# Revit family: FAMILLE_COMPOSABLE_MOSAIC_FR
name_source: partatom
category: Equipement électrique
revit_build: Autodesk Revit 2017 (Build: 20190508_0315(x64)
units: mm (PartAtom-declared; Revit-internal decimal feet)

## family parameters
Basée sur le plan de construction = Non
Configuration du panneau = Deux colonnes, circuits au sein
Cote de connecteur circulaire = Utiliser le diamètre
Couper avec des vides une fois chargée = Non
Partagée = Oui
Point de calcul de pièce = Non
Toujours verticalement = Oui
Type d'élément = Tableau de raccordement

## types (20) — shared parameters
FONCTION MODULE 1 = CACHE_FR : CACHE
FONCTION RANG 2 MODULE 11 = VIDE_FR

## per-type parameters (varying)
- Type 1 _ 1 Module: DECALAGE X=22.5 mm  [stored 0.0738189 ft]; FONCTION MODULE 10=VIDE_FR; FONCTION MODULE 11=VIDE_FR; FONCTION MODULE 2=VIDE_FR; FONCTION MODULE 3=VIDE_FR; FONCTION MODULE 4=VIDE_FR; FONCTION MODULE 5=VIDE_FR; FONCTION MODULE 6=VIDE_FR; FONCTION MODULE 7=VIDE_FR; FONCTION MODULE 8=VIDE_FR; FONCTION MODULE 9=VIDE_FR; FONCTION RANG 2 MODULE 1=VIDE_FR; FONCTION RANG 2 MODULE 10=VIDE_FR; FONCTION RANG 2 MODULE 2=VIDE_FR; FONCTION RANG 2 MODULE 3=VIDE_FR; FONCTION RANG 2 MODULE 4=VIDE_FR; FONCTION RANG 2 MODULE 5=VIDE_FR; FONCTION RANG 2 MODULE 6=VIDE_FR; FONCTION RANG 2 MODULE 7=VIDE_FR; FONCTION RANG 2 MODULE 8=VIDE_FR; FONCTION RANG 2 MODULE 9=VIDE_FR; FONCTION RANG 3 MODULE 1=VIDE_FR; FONCTION RANG 3 MODULE 2=VIDE_FR; PLAQUE=PLAQUES_MOSAIC_FR : LEGRAND_MOSAIC_PLAQUE_1_MOD_BLANC_078801L.rfa; SUPPORT=SUPPORTS_UNIVERSELS_FR : LEGRAND_BATIBOX_SUPPORT_1_MOD_080250.rfa
- Type 2 _ 2 Modules: DECALAGE X=45 mm  [stored 0.147638 ft]; FONCTION MODULE 10=VIDE_FR; FONCTION MODULE 11=VIDE_FR; FONCTION MODULE 2=CACHE_FR : CACHE; FONCTION MODULE 3=VIDE_FR; FONCTION MODULE 4=VIDE_FR; FONCTION MODULE 5=VIDE_FR; FONCTION MODULE 6=VIDE_FR; FONCTION MODULE 7=VIDE_FR; FONCTION MODULE 8=VIDE_FR; FONCTION MODULE 9=VIDE_FR; FONCTION RANG 2 MODULE 1=VIDE_FR; FONCTION RANG 2 MODULE 10=VIDE_FR; FONCTION RANG 2 MODULE 2=VIDE_FR; FONCTION RANG 2 MODULE 3=VIDE_FR; FONCTION RANG 2 MODULE 4=VIDE_FR; FONCTION RANG 2 MODULE 5=VIDE_FR; FONCTION RANG 2 MODULE 6=VIDE_FR; FONCTION RANG 2 MODULE 7=VIDE_FR; FONCTION RANG 2 MODULE 8=VIDE_FR; FONCTION RANG 2 MODULE 9=VIDE_FR; FONCTION RANG 3 MODULE 1=VIDE_FR; FONCTION RANG 3 MODULE 2=VIDE_FR; PLAQUE=PLAQUES_MOSAIC_FR : LEGRAND_MOSAIC_PLAQUE_2_MOD_BLANC_078802L.rfa; SUPPORT=SUPPORTS_UNIVERSELS_FR : LEGRAND_BATIBOX_SUPPORT_1_POSTE_2_MOD_080251.rfa H
- Type 3 _ 3 Modules: DECALAGE X=67.5 mm  [stored 0.221457 ft]; FONCTION MODULE 10=VIDE_FR; FONCTION MODULE 11=VIDE_FR; FONCTION MODULE 2=CACHE_FR : CACHE; FONCTION MODULE 3=CACHE_FR : CACHE; FONCTION MODULE 4=VIDE_FR; FONCTION MODULE 5=VIDE_FR; FONCTION MODULE 6=VIDE_FR; FONCTION MODULE 7=VIDE_FR; FONCTION MODULE 8=VIDE_FR; FONCTION MODULE 9=VIDE_FR; FONCTION RANG 2 MODULE 1=VIDE_FR; FONCTION RANG 2 MODULE 10=VIDE_FR; FONCTION RANG 2 MODULE 2=VIDE_FR; FONCTION RANG 2 MODULE 3=VIDE_FR; FONCTION RANG 2 MODULE 4=VIDE_FR; FONCTION RANG 2 MODULE 5=VIDE_FR; FONCTION RANG 2 MODULE 6=VIDE_FR; FONCTION RANG 2 MODULE 7=VIDE_FR; FONCTION RANG 2 MODULE 8=VIDE_FR; FONCTION RANG 2 MODULE 9=VIDE_FR; FONCTION RANG 3 MODULE 1=VIDE_FR; FONCTION RANG 3 MODULE 2=VIDE_FR; PLAQUE=PLAQUES_MOSAIC_FR : LEGRAND_MOSAIC_PLAQUE_3_MOD_BLANC_078803L.rfa; SUPPORT=SUPPORTS_UNIVERSELS_FR : LEGRAND_BATIBOX_SUPPORT_3_MOD_080259.rfa H
- Type 4  _ 4 Modules: DECALAGE X=101.255 mm  [stored 0.332201 ft]; FONCTION MODULE 10=VIDE_FR; FONCTION MODULE 11=VIDE_FR; FONCTION MODULE 2=CACHE_FR : CACHE; FONCTION MODULE 3=CACHE_FR : CACHE; FONCTION MODULE 4=CACHE_FR : CACHE; FONCTION MODULE 5=VIDE_FR; FONCTION MODULE 6=VIDE_FR; FONCTION MODULE 7=VIDE_FR; FONCTION MODULE 8=VIDE_FR; FONCTION MODULE 9=VIDE_FR; FONCTION RANG 2 MODULE 1=VIDE_FR; FONCTION RANG 2 MODULE 10=VIDE_FR; FONCTION RANG 2 MODULE 2=VIDE_FR; FONCTION RANG 2 MODULE 3=VIDE_FR; FONCTION RANG 2 MODULE 4=VIDE_FR; FONCTION RANG 2 MODULE 5=VIDE_FR; FONCTION RANG 2 MODULE 6=VIDE_FR; FONCTION RANG 2 MODULE 7=VIDE_FR; FONCTION RANG 2 MODULE 8=VIDE_FR; FONCTION RANG 2 MODULE 9=VIDE_FR; FONCTION RANG 3 MODULE 1=VIDE_FR; FONCTION RANG 3 MODULE 2=VIDE_FR; PLAQUE=PLAQUES_MOSAIC_FR : LEGRAND_MOSAIC_PLAQUE_4_MOD_BLANC_078814L.rfa; SUPPORT=SUPPORTS_UNIVERSELS_FR : LEGRAND_BATIBOX_SUPPORT_2_POSTES_4_5_MOD_080252.rfa H
- Type 5  _ 5 Modules: DECALAGE X=112.5 mm  [stored 0.369094 ft]; FONCTION MODULE 10=VIDE_FR; FONCTION MODULE 11=VIDE_FR; FONCTION MODULE 2=CACHE_FR : CACHE; FONCTION MODULE 3=CACHE_FR : CACHE; FONCTION MODULE 4=CACHE_FR : CACHE; FONCTION MODULE 5=CACHE_FR : CACHE; FONCTION MODULE 6=VIDE_FR; FONCTION MODULE 7=VIDE_FR; FONCTION MODULE 8=VIDE_FR; FONCTION MODULE 9=VIDE_FR; FONCTION RANG 2 MODULE 1=VIDE_FR; FONCTION RANG 2 MODULE 10=VIDE_FR; FONCTION RANG 2 MODULE 2=VIDE_FR; FONCTION RANG 2 MODULE 3=VIDE_FR; FONCTION RANG 2 MODULE 4=VIDE_FR; FONCTION RANG 2 MODULE 5=VIDE_FR; FONCTION RANG 2 MODULE 6=VIDE_FR; FONCTION RANG 2 MODULE 7=VIDE_FR; FONCTION RANG 2 MODULE 8=VIDE_FR; FONCTION RANG 2 MODULE 9=VIDE_FR; FONCTION RANG 3 MODULE 1=VIDE_FR; FONCTION RANG 3 MODULE 2=VIDE_FR; PLAQUE=PLAQUES_MOSAIC_FR : LEGRAND_MOSAIC_PLAQUE_5_MOD_BLANC_078815L.rfa; SUPPORT=SUPPORTS_UNIVERSELS_FR : LEGRAND_BATIBOX_SUPPORT_2_POSTES_4_5_MOD_080252.rfa H
- Type 6 _ 2x2 Modules: DECALAGE X=112.5 mm  [stored 0.369094 ft]; FONCTION MODULE 10=VIDE_FR; FONCTION MODULE 11=VIDE_FR; FONCTION MODULE 2=CACHE_FR : CACHE; FONCTION MODULE 3=VIDE_FR; FONCTION MODULE 4=CACHE_FR : CACHE; FONCTION MODULE 5=CACHE_FR : CACHE; FONCTION MODULE 6=VIDE_FR; FONCTION MODULE 7=VIDE_FR; FONCTION MODULE 8=VIDE_FR; FONCTION MODULE 9=VIDE_FR; FONCTION RANG 2 MODULE 1=VIDE_FR; FONCTION RANG 2 MODULE 10=VIDE_FR; FONCTION RANG 2 MODULE 2=VIDE_FR; FONCTION RANG 2 MODULE 3=VIDE_FR; FONCTION RANG 2 MODULE 4=VIDE_FR; FONCTION RANG 2 MODULE 5=VIDE_FR; FONCTION RANG 2 MODULE 6=VIDE_FR; FONCTION RANG 2 MODULE 7=VIDE_FR; FONCTION RANG 2 MODULE 8=VIDE_FR; FONCTION RANG 2 MODULE 9=VIDE_FR; FONCTION RANG 3 MODULE 1=VIDE_FR; FONCTION RANG 3 MODULE 2=VIDE_FR; PLAQUE=PLAQUES_MOSAIC_FR : LEGRAND_MOSAIC_PLAQUE_2X2_MOD_BLANC_078804L.rfa; SUPPORT=SUPPORTS_UNIVERSELS_FR : LEGRAND_BATIBOX_SUPPORT_2_POSTES_4_5_MOD_080252.rfa H
- Type 9 _ 6 Modules: DECALAGE X=157.5 mm  [stored 0.516732 ft]; FONCTION MODULE 10=VIDE_FR; FONCTION MODULE 11=VIDE_FR; FONCTION MODULE 2=CACHE_FR : CACHE; FONCTION MODULE 3=CACHE_FR : CACHE; FONCTION MODULE 4=CACHE_FR : CACHE; FONCTION MODULE 5=CACHE_FR : CACHE; FONCTION MODULE 6=CACHE_FR : CACHE; FONCTION MODULE 7=VIDE_FR; FONCTION MODULE 8=VIDE_FR; FONCTION MODULE 9=VIDE_FR; FONCTION RANG 2 MODULE 1=VIDE_FR; FONCTION RANG 2 MODULE 10=VIDE_FR; FONCTION RANG 2 MODULE 2=VIDE_FR; FONCTION RANG 2 MODULE 3=VIDE_FR; FONCTION RANG 2 MODULE 4=VIDE_FR; FONCTION RANG 2 MODULE 5=VIDE_FR; FONCTION RANG 2 MODULE 6=VIDE_FR; FONCTION RANG 2 MODULE 7=VIDE_FR; FONCTION RANG 2 MODULE 8=VIDE_FR; FONCTION RANG 2 MODULE 9=VIDE_FR; FONCTION RANG 3 MODULE 1=VIDE_FR; FONCTION RANG 3 MODULE 2=VIDE_FR; PLAQUE=PLAQUES_MOSAIC_FR : LEGRAND_MOSAIC_PLAQUE_6_MOD_BLANC_078816L.rfa; SUPPORT=SUPPORTS_UNIVERSELS_FR : LEGRAND_BATIBOX_SUPPORT_3_POSTES_6_8_MOD_080253.rfa H
- Type. 10 _ 8 Modules: DECALAGE X=180 mm  [stored 0.590551 ft]; FONCTION MODULE 10=VIDE_FR; FONCTION MODULE 11=VIDE_FR; FONCTION MODULE 2=CACHE_FR : CACHE; FONCTION MODULE 3=CACHE_FR : CACHE; FONCTION MODULE 4=CACHE_FR : CACHE; FONCTION MODULE 5=CACHE_FR : CACHE; FONCTION MODULE 6=CACHE_FR : CACHE; FONCTION MODULE 7=CACHE_FR : CACHE; FONCTION MODULE 8=CACHE_FR : CACHE; FONCTION MODULE 9=VIDE_FR; FONCTION RANG 2 MODULE 1=VIDE_FR; FONCTION RANG 2 MODULE 10=VIDE_FR; FONCTION RANG 2 MODULE 2=VIDE_FR; FONCTION RANG 2 MODULE 3=VIDE_FR; FONCTION RANG 2 MODULE 4=VIDE_FR; FONCTION RANG 2 MODULE 5=VIDE_FR; FONCTION RANG 2 MODULE 6=VIDE_FR; FONCTION RANG 2 MODULE 7=VIDE_FR; FONCTION RANG 2 MODULE 8=VIDE_FR; FONCTION RANG 2 MODULE 9=VIDE_FR; FONCTION RANG 3 MODULE 1=VIDE_FR; FONCTION RANG 3 MODULE 2=VIDE_FR; PLAQUE=PLAQUES_MOSAIC_FR : LEGRAND_MOSAIC_PLAQUE_8_MOD_BLANC_078818L.rfa; SUPPORT=SUPPORTS_UNIVERSELS_FR : LEGRAND_BATIBOX_SUPPORT_3_POSTES_6_8_MOD_080253.rfa H
- Type. 11 _ 3x2 Modules: DECALAGE X=180 mm  [stored 0.590551 ft]; FONCTION MODULE 10=VIDE_FR; FONCTION MODULE 11=VIDE_FR; FONCTION MODULE 2=CACHE_FR : CACHE; FONCTION MODULE 3=VIDE_FR; FONCTION MODULE 4=CACHE_FR : CACHE; FONCTION MODULE 5=CACHE_FR : CACHE; FONCTION MODULE 6=VIDE_FR; FONCTION MODULE 7=CACHE_FR : CACHE; FONCTION MODULE 8=CACHE_FR : CACHE; FONCTION MODULE 9=VIDE_FR; FONCTION RANG 2 MODULE 1=VIDE_FR; FONCTION RANG 2 MODULE 10=VIDE_FR; FONCTION RANG 2 MODULE 2=VIDE_FR; FONCTION RANG 2 MODULE 3=VIDE_FR; FONCTION RANG 2 MODULE 4=VIDE_FR; FONCTION RANG 2 MODULE 5=VIDE_FR; FONCTION RANG 2 MODULE 6=VIDE_FR; FONCTION RANG 2 MODULE 7=VIDE_FR; FONCTION RANG 2 MODULE 8=VIDE_FR; FONCTION RANG 2 MODULE 9=VIDE_FR; FONCTION RANG 3 MODULE 1=VIDE_FR; FONCTION RANG 3 MODULE 2=VIDE_FR; PLAQUE=PLAQUES_MOSAIC_FR : LEGRAND_MOSAIC_PLAQUE_3X2_MOD_BLANC_078806L.rfa; SUPPORT=SUPPORTS_UNIVERSELS_FR : LEGRAND_BATIBOX_SUPPORT_3_POSTES_6_8_MOD_080253.rfa H
- Type. 13 _ 10 Modules: DECALAGE X=237.25 mm  [stored 0.778379 ft]; FONCTION MODULE 10=CACHE_FR : CACHE; FONCTION MODULE 11=VIDE_FR; FONCTION MODULE 2=CACHE_FR : CACHE; FONCTION MODULE 3=CACHE_FR : CACHE; FONCTION MODULE 4=CACHE_FR : CACHE; FONCTION MODULE 5=CACHE_FR : CACHE; FONCTION MODULE 6=CACHE_FR : CACHE; FONCTION MODULE 7=CACHE_FR : CACHE; FONCTION MODULE 8=CACHE_FR : CACHE; FONCTION MODULE 9=CACHE_FR : CACHE; FONCTION RANG 2 MODULE 1=VIDE_FR; FONCTION RANG 2 MODULE 10=VIDE_FR; FONCTION RANG 2 MODULE 2=VIDE_FR; FONCTION RANG 2 MODULE 3=VIDE_FR; FONCTION RANG 2 MODULE 4=VIDE_FR; FONCTION RANG 2 MODULE 5=VIDE_FR; FONCTION RANG 2 MODULE 6=VIDE_FR; FONCTION RANG 2 MODULE 7=VIDE_FR; FONCTION RANG 2 MODULE 8=VIDE_FR; FONCTION RANG 2 MODULE 9=VIDE_FR; FONCTION RANG 3 MODULE 1=VIDE_FR; FONCTION RANG 3 MODULE 2=VIDE_FR; PLAQUE=PLAQUES_MOSAIC_FR : LEGRAND_MOSAIC_PLAQUE_10_MOD_BLANC_078810L.rfa; SUPPORT=SUPPORTS_UNIVERSELS_FR : LEGRAND_BATIBOX_SUPPORT_4_POSTES_10_MOD_080254.rfa H
- Type. 14 _ 4x2 Modules: DECALAGE X=247.5 mm  [stored 0.812008 ft]; FONCTION MODULE 10=CACHE_FR : CACHE; FONCTION MODULE 11=CACHE_FR : CACHE; FONCTION MODULE 2=CACHE_FR : CACHE; FONCTION MODULE 3=VIDE_FR; FONCTION MODULE 4=CACHE_FR : CACHE; FONCTION MODULE 5=CACHE_FR : CACHE; FONCTION MODULE 6=VIDE_FR; FONCTION MODULE 7=CACHE_FR : CACHE; FONCTION MODULE 8=CACHE_FR : CACHE; FONCTION MODULE 9=VIDE_FR; FONCTION RANG 2 MODULE 1=VIDE_FR; FONCTION RANG 2 MODULE 10=VIDE_FR; FONCTION RANG 2 MODULE 2=VIDE_FR; FONCTION RANG 2 MODULE 3=VIDE_FR; FONCTION RANG 2 MODULE 4=VIDE_FR; FONCTION RANG 2 MODULE 5=VIDE_FR; FONCTION RANG 2 MODULE 6=VIDE_FR; FONCTION RANG 2 MODULE 7=VIDE_FR; FONCTION RANG 2 MODULE 8=VIDE_FR; FONCTION RANG 2 MODULE 9=VIDE_FR; FONCTION RANG 3 MODULE 1=VIDE_FR; FONCTION RANG 3 MODULE 2=VIDE_FR; PLAQUE=PLAQUES_MOSAIC_FR : LEGRAND_MOSAIC_PLAQUE_4X2_MOD_BLANC_078808L.rfa; SUPPORT=SUPPORTS_UNIVERSELS_FR : LEGRAND_BATIBOX_SUPPORT_4_POSTES_10_MOD_080254.rfa H
- Type. 15 _ 2x5 Modules: DECALAGE X=112.5 mm  [stored 0.369094 ft]; FONCTION MODULE 10=VIDE_FR; FONCTION MODULE 11=VIDE_FR; FONCTION MODULE 2=CACHE_FR : CACHE; FONCTION MODULE 3=CACHE_FR : CACHE; FONCTION MODULE 4=CACHE_FR : CACHE; FONCTION MODULE 5=CACHE_FR : CACHE; FONCTION MODULE 6=VIDE_FR; FONCTION MODULE 7=VIDE_FR; FONCTION MODULE 8=VIDE_FR; FONCTION MODULE 9=VIDE_FR; FONCTION RANG 2 MODULE 1=CACHE_FR : CACHE; FONCTION RANG 2 MODULE 10=VIDE_FR; FONCTION RANG 2 MODULE 2=CACHE_FR : CACHE; FONCTION RANG 2 MODULE 3=CACHE_FR : CACHE; FONCTION RANG 2 MODULE 4=CACHE_FR : CACHE; FONCTION RANG 2 MODULE 5=CACHE_FR : CACHE; FONCTION RANG 2 MODULE 6=VIDE_FR; FONCTION RANG 2 MODULE 7=VIDE_FR; FONCTION RANG 2 MODULE 8=VIDE_FR; FONCTION RANG 2 MODULE 9=VIDE_FR; FONCTION RANG 3 MODULE 1=VIDE_FR; FONCTION RANG 3 MODULE 2=VIDE_FR; PLAQUE=PLAQUES_MOSAIC_FR : LEGRAND_MOSAIC_PLAQUE_2X5_MOD_BLANC_078830L.rfa; SUPPORT=SUPPORTS_UNIVERSELS_FR : LEGRAND_BATIBOX_SUPPORT_2X2_POSTES_2X4_5_MOD_080264.rfa H
- Type. 16 _ 2x2x2 Modules: DECALAGE X=112.5 mm  [stored 0.369094 ft]; FONCTION MODULE 10=VIDE_FR; FONCTION MODULE 11=VIDE_FR; FONCTION MODULE 2=CACHE_FR : CACHE; FONCTION MODULE 3=VIDE_FR; FONCTION MODULE 4=CACHE_FR : CACHE; FONCTION MODULE 5=CACHE_FR : CACHE; FONCTION MODULE 6=VIDE_FR; FONCTION MODULE 7=VIDE_FR; FONCTION MODULE 8=VIDE_FR; FONCTION MODULE 9=VIDE_FR; FONCTION RANG 2 MODULE 1=CACHE_FR : CACHE; FONCTION RANG 2 MODULE 10=VIDE_FR; FONCTION RANG 2 MODULE 2=CACHE_FR : CACHE; FONCTION RANG 2 MODULE 3=VIDE_FR; FONCTION RANG 2 MODULE 4=CACHE_FR : CACHE; FONCTION RANG 2 MODULE 5=CACHE_FR : CACHE; FONCTION RANG 2 MODULE 6=VIDE_FR; FONCTION RANG 2 MODULE 7=VIDE_FR; FONCTION RANG 2 MODULE 8=VIDE_FR; FONCTION RANG 2 MODULE 9=VIDE_FR; FONCTION RANG 3 MODULE 1=VIDE_FR; FONCTION RANG 3 MODULE 2=VIDE_FR; PLAQUE=PLAQUES_MOSAIC_FR : LEGRAND_MOSAIC_PLAQUE_2X2X2_MOD_BLANC_078838L.rfa; SUPPORT=SUPPORTS_UNIVERSELS_FR : LEGRAND_BATIBOX_SUPPORT_2X2_POSTES_2X4_5_MOD_080264.rfa H
- Type. 17 _ 2x6 Modules: DECALAGE X=157.5 mm  [stored 0.516732 ft]; FONCTION MODULE 10=VIDE_FR; FONCTION MODULE 11=VIDE_FR; FONCTION MODULE 2=CACHE_FR : CACHE; FONCTION MODULE 3=CACHE_FR : CACHE; FONCTION MODULE 4=CACHE_FR : CACHE; FONCTION MODULE 5=CACHE_FR : CACHE; FONCTION MODULE 6=CACHE_FR : CACHE; FONCTION MODULE 7=VIDE_FR; FONCTION MODULE 8=VIDE_FR; FONCTION MODULE 9=VIDE_FR; FONCTION RANG 2 MODULE 1=CACHE_FR : CACHE; FONCTION RANG 2 MODULE 10=VIDE_FR; FONCTION RANG 2 MODULE 2=CACHE_FR : CACHE; FONCTION RANG 2 MODULE 3=CACHE_FR : CACHE; FONCTION RANG 2 MODULE 4=CACHE_FR : CACHE; FONCTION RANG 2 MODULE 5=CACHE_FR : CACHE; FONCTION RANG 2 MODULE 6=CACHE_FR : CACHE; FONCTION RANG 2 MODULE 7=VIDE_FR; FONCTION RANG 2 MODULE 8=VIDE_FR; FONCTION RANG 2 MODULE 9=VIDE_FR; FONCTION RANG 3 MODULE 1=VIDE_FR; FONCTION RANG 3 MODULE 2=VIDE_FR; PLAQUE=PLAQUES_MOSAIC_FR : LEGRAND_MOSAIC_PLAQUE_2X6_MOD_BLANC_078836L.rfa; SUPPORT=SUPPORTS_UNIVERSELS_FR : LEGRAND_BATIBOX_SUPPORT_2X3_POSTES_2X6_8_MOD_080266.rfa H
- Type. 18 _ 2x3x2 Modules: DECALAGE X=180 mm  [stored 0.590551 ft]; FONCTION MODULE 10=VIDE_FR; FONCTION MODULE 11=VIDE_FR; FONCTION MODULE 2=CACHE_FR : CACHE; FONCTION MODULE 3=VIDE_FR; FONCTION MODULE 4=CACHE_FR : CACHE; FONCTION MODULE 5=CACHE_FR : CACHE; FONCTION MODULE 6=VIDE_FR; FONCTION MODULE 7=CACHE_FR : CACHE; FONCTION MODULE 8=CACHE_FR : CACHE; FONCTION MODULE 9=VIDE_FR; FONCTION RANG 2 MODULE 1=CACHE_FR : CACHE; FONCTION RANG 2 MODULE 10=VIDE_FR; FONCTION RANG 2 MODULE 2=CACHE_FR : CACHE; FONCTION RANG 2 MODULE 3=VIDE_FR; FONCTION RANG 2 MODULE 4=CACHE_FR : CACHE; FONCTION RANG 2 MODULE 5=CACHE_FR : CACHE; FONCTION RANG 2 MODULE 6=VIDE_FR; FONCTION RANG 2 MODULE 7=CACHE_FR : CACHE; FONCTION RANG 2 MODULE 8=CACHE_FR : CACHE; FONCTION RANG 2 MODULE 9=VIDE_FR; FONCTION RANG 3 MODULE 1=VIDE_FR; FONCTION RANG 3 MODULE 2=VIDE_FR; PLAQUE=PLAQUES_MOSAIC_FR : LEGRAND_MOSAIC_PLAQUE_2X3X2_MOD_BLANC_078832L.rfa; SUPPORT=SUPPORTS_UNIVERSELS_FR : LEGRAND_BATIBOX_SUPPORT_2X3_POSTES_2X6_8_MOD_080266.rfa H
- Type. 19 _ 2x8 Modules: DECALAGE X=180 mm  [stored 0.590551 ft]; FONCTION MODULE 10=VIDE_FR; FONCTION MODULE 11=VIDE_FR; FONCTION MODULE 2=CACHE_FR : CACHE; FONCTION MODULE 3=CACHE_FR : CACHE; FONCTION MODULE 4=CACHE_FR : CACHE; FONCTION MODULE 5=CACHE_FR : CACHE; FONCTION MODULE 6=CACHE_FR : CACHE; FONCTION MODULE 7=CACHE_FR : CACHE; FONCTION MODULE 8=CACHE_FR : CACHE; FONCTION MODULE 9=VIDE_FR; FONCTION RANG 2 MODULE 1=CACHE_FR : CACHE; FONCTION RANG 2 MODULE 10=VIDE_FR; FONCTION RANG 2 MODULE 2=CACHE_FR : CACHE; FONCTION RANG 2 MODULE 3=CACHE_FR : CACHE; FONCTION RANG 2 MODULE 4=CACHE_FR : CACHE; FONCTION RANG 2 MODULE 5=CACHE_FR : CACHE; FONCTION RANG 2 MODULE 6=CACHE_FR : CACHE; FONCTION RANG 2 MODULE 7=CACHE_FR : CACHE; FONCTION RANG 2 MODULE 8=CACHE_FR : CACHE; FONCTION RANG 2 MODULE 9=VIDE_FR; FONCTION RANG 3 MODULE 1=VIDE_FR; FONCTION RANG 3 MODULE 2=VIDE_FR; PLAQUE=PLAQUES_MOSAIC_FR : LEGRAND_MOSAIC_PLAQUE_2X8_MOD_BLANC_078837L.rfa; SUPPORT=SUPPORTS_UNIVERSELS_FR : LEGRAND_BATIBOX_SUPPORT_2X3_POSTES_2X6_8_MOD_080266.rfa H
- Type. 20 _ 2x10 Modules: DECALAGE X=225 mm  [stored 0.738189 ft]; FONCTION MODULE 10=CACHE_FR : CACHE; FONCTION MODULE 11=VIDE_FR; FONCTION MODULE 2=CACHE_FR : CACHE; FONCTION MODULE 3=CACHE_FR : CACHE; FONCTION MODULE 4=CACHE_FR : CACHE; FONCTION MODULE 5=CACHE_FR : CACHE; FONCTION MODULE 6=CACHE_FR : CACHE; FONCTION MODULE 7=CACHE_FR : CACHE; FONCTION MODULE 8=CACHE_FR : CACHE; FONCTION MODULE 9=CACHE_FR : CACHE; FONCTION RANG 2 MODULE 1=CACHE_FR : CACHE; FONCTION RANG 2 MODULE 10=CACHE_FR : CACHE; FONCTION RANG 2 MODULE 2=CACHE_FR : CACHE; FONCTION RANG 2 MODULE 3=CACHE_FR : CACHE; FONCTION RANG 2 MODULE 4=CACHE_FR : CACHE; FONCTION RANG 2 MODULE 5=CACHE_FR : CACHE; FONCTION RANG 2 MODULE 6=CACHE_FR : CACHE; FONCTION RANG 2 MODULE 7=CACHE_FR : CACHE; FONCTION RANG 2 MODULE 8=CACHE_FR : CACHE; FONCTION RANG 2 MODULE 9=CACHE_FR : CACHE; FONCTION RANG 3 MODULE 1=VIDE_FR; FONCTION RANG 3 MODULE 2=VIDE_FR; PLAQUE=PLAQUES_MOSAIC_FR : LEGRAND_MOSAIC_PLAQUE_2X10_MOD_BLANC_078828L.rfa; SUPPORT=SUPPORTS_UNIVERSELS_FR : LEGRAND_BATIBOX_SUPPORT_2X10_MOD_080268.rfa H
- Type 7 _ 5 Modules Vertical: DECALAGE X=45 mm  [stored 0.147638 ft]; FONCTION MODULE 10=VIDE_FR; FONCTION MODULE 11=VIDE_FR; FONCTION MODULE 2=CACHE_FR : CACHE; FONCTION MODULE 3=VIDE_FR; FONCTION MODULE 4=VIDE_FR; FONCTION MODULE 5=VIDE_FR; FONCTION MODULE 6=VIDE_FR; FONCTION MODULE 7=VIDE_FR; FONCTION MODULE 8=VIDE_FR; FONCTION MODULE 9=VIDE_FR; FONCTION RANG 2 MODULE 1=CACHE_FR : CACHE; FONCTION RANG 2 MODULE 10=VIDE_FR; FONCTION RANG 2 MODULE 2=CACHE_FR : CACHE; FONCTION RANG 2 MODULE 3=VIDE_FR; FONCTION RANG 2 MODULE 4=VIDE_FR; FONCTION RANG 2 MODULE 5=VIDE_FR; FONCTION RANG 2 MODULE 6=VIDE_FR; FONCTION RANG 2 MODULE 7=VIDE_FR; FONCTION RANG 2 MODULE 8=VIDE_FR; FONCTION RANG 2 MODULE 9=VIDE_FR; FONCTION RANG 3 MODULE 1=VIDE_FR; FONCTION RANG 3 MODULE 2=VIDE_FR; PLAQUE=PLAQUES_MOSAIC_FR : LEGRAND_MOSAIC_PLAQUE_5_MOD_VERTICAL_BLANC_078825L.rfa; SUPPORT=SUPPORTS_UNIVERSELS_FR : LEGRAND_BATIBOX_SUPPORT_2_POSTES_4_5_MOD_080252.rfa V
- Type 8 _ 2x2 Modules Vertical: DECALAGE X=45 mm  [stored 0.147638 ft]; FONCTION MODULE 10=VIDE_FR; FONCTION MODULE 11=VIDE_FR; FONCTION MODULE 2=CACHE_FR : CACHE; FONCTION MODULE 3=VIDE_FR; FONCTION MODULE 4=VIDE_FR; FONCTION MODULE 5=VIDE_FR; FONCTION MODULE 6=VIDE_FR; FONCTION MODULE 7=VIDE_FR; FONCTION MODULE 8=VIDE_FR; FONCTION MODULE 9=VIDE_FR; FONCTION RANG 2 MODULE 1=CACHE_FR : CACHE; FONCTION RANG 2 MODULE 10=VIDE_FR; FONCTION RANG 2 MODULE 2=CACHE_FR : CACHE; FONCTION RANG 2 MODULE 3=VIDE_FR; FONCTION RANG 2 MODULE 4=VIDE_FR; FONCTION RANG 2 MODULE 5=VIDE_FR; FONCTION RANG 2 MODULE 6=VIDE_FR; FONCTION RANG 2 MODULE 7=VIDE_FR; FONCTION RANG 2 MODULE 8=VIDE_FR; FONCTION RANG 2 MODULE 9=VIDE_FR; FONCTION RANG 3 MODULE 1=VIDE_FR; FONCTION RANG 3 MODULE 2=VIDE_FR; PLAQUE=PLAQUES_MOSAIC_FR : LEGRAND_MOSAIC_PLAQUE_2X2_MOD_VERTICAL_BLANC_078822L.rfa; SUPPORT=SUPPORTS_UNIVERSELS_FR : LEGRAND_BATIBOX_SUPPORT_2_POSTES_4_5_MOD_080252.rfa V
- Type. 12 _ 3x2 Modules Vertical: DECALAGE X=45 mm  [stored 0.147638 ft]; FONCTION MODULE 10=VIDE_FR; FONCTION MODULE 11=VIDE_FR; FONCTION MODULE 2=CACHE_FR : CACHE; FONCTION MODULE 3=VIDE_FR; FONCTION MODULE 4=VIDE_FR; FONCTION MODULE 5=VIDE_FR; FONCTION MODULE 6=VIDE_FR; FONCTION MODULE 7=VIDE_FR; FONCTION MODULE 8=VIDE_FR; FONCTION MODULE 9=VIDE_FR; FONCTION RANG 2 MODULE 1=CACHE_FR : CACHE; FONCTION RANG 2 MODULE 10=VIDE_FR; FONCTION RANG 2 MODULE 2=CACHE_FR : CACHE; FONCTION RANG 2 MODULE 3=VIDE_FR; FONCTION RANG 2 MODULE 4=VIDE_FR; FONCTION RANG 2 MODULE 5=VIDE_FR; FONCTION RANG 2 MODULE 6=VIDE_FR; FONCTION RANG 2 MODULE 7=VIDE_FR; FONCTION RANG 2 MODULE 8=VIDE_FR; FONCTION RANG 2 MODULE 9=VIDE_FR; FONCTION RANG 3 MODULE 1=CACHE_FR : CACHE; FONCTION RANG 3 MODULE 2=CACHE_FR : CACHE; PLAQUE=PLAQUES_MOSAIC_FR : LEGRAND_MOSAIC_PLAQUE_3X2_MOD_VERTICAL_BLANC_078823L.rfa; SUPPORT=SUPPORTS_UNIVERSELS_FR : LEGRAND_BATIBOX_SUPPORT_3_POSTES_6_8_MOD_080253.rfa V

note: [stored X ft] marks values corroborated as IEEE doubles in the binary element streams (Revit-internal decimal feet)
